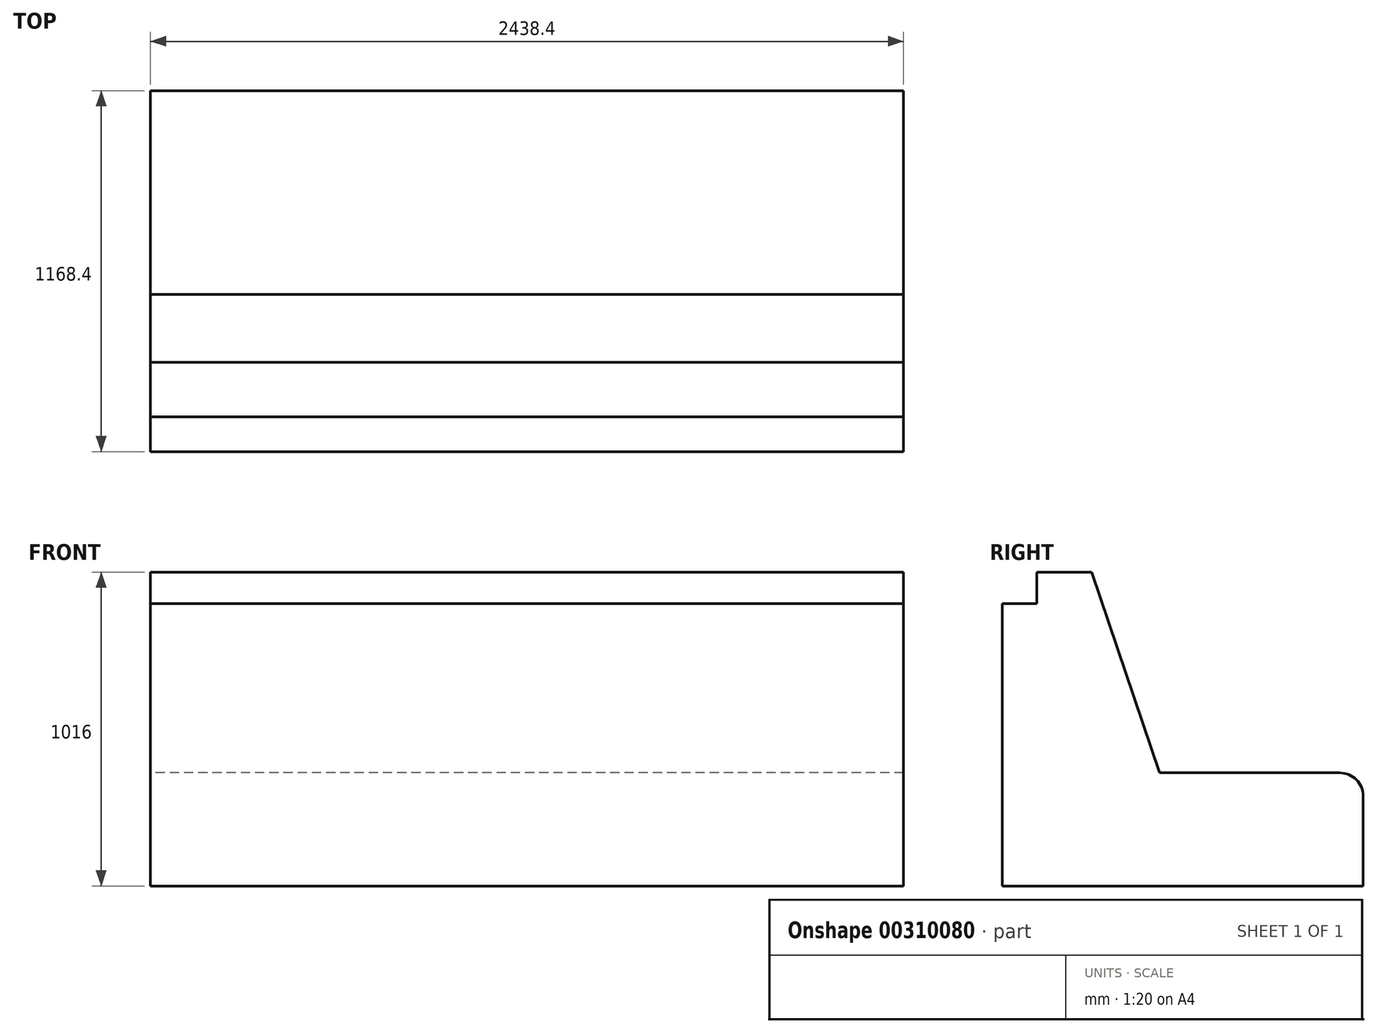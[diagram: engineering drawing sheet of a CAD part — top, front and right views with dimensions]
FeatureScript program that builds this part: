
annotation { "Feature Type Name" : "Feature", "Feature Type Description" : "" }
export const myFeature = defineFeature(function(context is Context, id is Id, definition is map)
    precondition{}
    {
        {
            var Q0;
            Q0=qCreatedBy(makeId("Right.planeOp"),FACE);
            var sketch = newSketch(context, id + "F0", { "sketchPlane" : qUnion([Q0])});
            skLineSegment(sketch, "E0.bottom", {"start": v(0, 914.4) * mm, "end": v(111.87, 914.4) * mm});
            skLineSegment(sketch, "E0.top", {"start": v(0, 0) * mm, "end": v(1168.4, 0) * mm});
            skLineSegment(sketch, "E0.left", {"start": v(0, 914.4) * mm, "end": v(0, 0) * mm});
            skLineSegment(sketch, "E0.right", {"start": v(1168.4, 289.75) * mm, "end": v(1168.4, 0) * mm});
            skLineSegment(sketch, "E1", {"start": v(111.87, 914.4) * mm, "end": v(111.87, 1016) * mm});
            skLineSegment(sketch, "E2", {"start": v(111.87, 1016) * mm, "end": v(289.07, 1016) * mm});
            skLineSegment(sketch, "E3", {"start": v(289.07, 1016) * mm, "end": v(508.63, 365.95) * mm});
            skLineSegment(sketch, "E4", {"start": v(508.63, 365.95) * mm, "end": v(1092.2, 365.95) * mm});
            skPoint(sketch, "E5.visualSharp", {"position": v(1168.4, 365.95) * mm});
            skArc(sketch, "E5.filletArc", {"start": v(1168.4, 289.75) * mm, "mid": v(1146.08, 343.63) * mm, "end": v(1092.2, 365.95) * mm});
            skSolve(sketch);
        }
        {
            var Q0;
            Q0 = qSketchRegion(id + "F0", true);
            extrude(context, id + "F1", {"entities" : qUnion([Q0]), "depth" : 2438.4 * mm});
        }
    });
